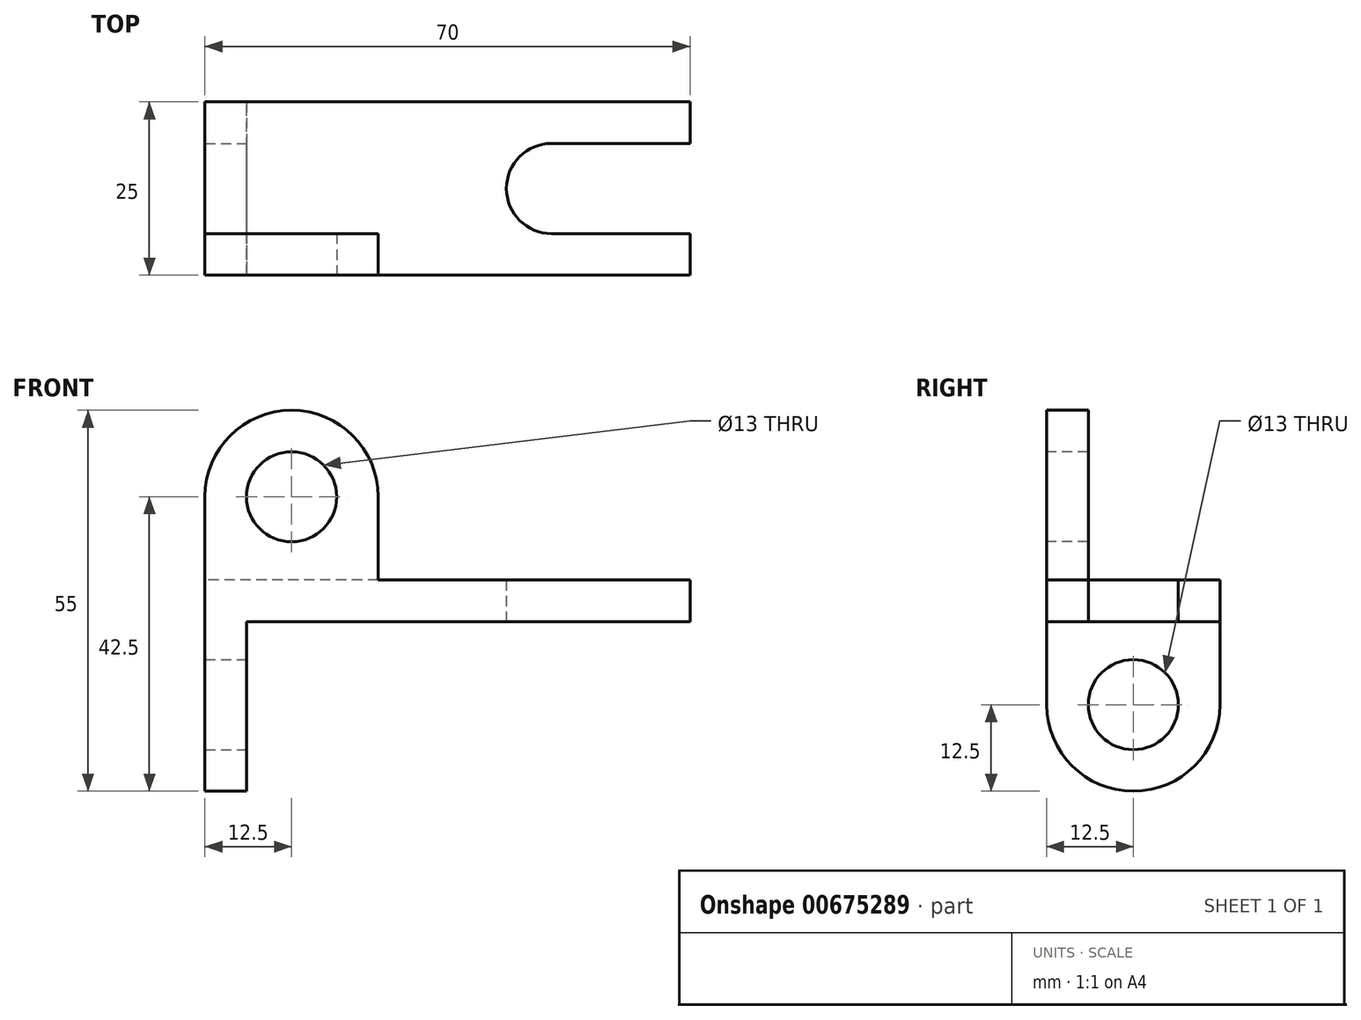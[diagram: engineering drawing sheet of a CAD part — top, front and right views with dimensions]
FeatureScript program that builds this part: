
annotation { "Feature Type Name" : "Feature", "Feature Type Description" : "" }
export const myFeature = defineFeature(function(context is Context, id is Id, definition is map)
    precondition{}
    {
        {
            var Q0;
            Q0=qCreatedBy(makeId("Top.planeOp"),FACE);
            var sketch = newSketch(context, id + "F0", { "sketchPlane" : qUnion([Q0])});
            skLineSegment(sketch, "E0.bottom", {"start": v(32, -12.5) * mm, "end": v(-32, -12.5) * mm});
            skLineSegment(sketch, "E0.top", {"start": v(32, 12.5) * mm, "end": v(-32, 12.5) * mm});
            skLineSegment(sketch, "E0.left", {"start": v(32, -12.5) * mm, "end": v(32, 12.5) * mm});
            skLineSegment(sketch, "E0.right", {"start": v(-32, -12.5) * mm, "end": v(-32, 12.5) * mm});
            skPoint(sketch, "E0.middle", {"position": v(0, 0) * mm});
            skLineSegment(sketch, "E1.bottom", {"start": v(32, -6.5) * mm, "end": v(12, -6.5) * mm});
            skLineSegment(sketch, "E1.top", {"start": v(32, 6.5) * mm, "end": v(12, 6.5) * mm});
            skLineSegment(sketch, "E1.left", {"start": v(32, -6.5) * mm, "end": v(32, 6.5) * mm});
            skLineSegment(sketch, "E1.right", {"start": v(12, -6.5) * mm, "end": v(12, 6.5) * mm});
            skPoint(sketch, "E1.middle", {"position": v(22, 0) * mm});
            skCircle(sketch, "E2", {"center": v(12, 0) * mm, "radius": 6.5 * mm});
            skSolve(sketch);
        }
        {
            var Q0;
            {var subQ4=sQuery(id+"F0.wireOp",EDGE,"E0.bottom");Q0=makeQuery(id+"F0.imprint","IMPRINT",FACE,{"disambiguationData":[TD([[makeQuery(id+"F0.imprint","IMPRINT",EDGE,{"derivedFrom":subQ4}),-1.0]])]});}
            extrude(context, id + "F1", {"entities" : qUnion([Q0]), "depth" : 6 * mm, "offsetDistance" : 25 * mm});
        }
        {
            var Q0;
            Q0=makeQuery(id+"F1.opExtrude","SWEPT_FACE",FACE,{"disambiguationData":[OSD([sQuery(id+"F0.wireOp",EDGE,"E0.right")])]});
            var sketch = newSketch(context, id + "F2", { "sketchPlane" : qUnion([Q0])});
            skLineSegment(sketch, "E3.bottom", {"start": v(-12.5, 6) * mm, "end": v(12.5, 6) * mm});
            skLineSegment(sketch, "E3.top", {"start": v(-12.5, -12) * mm, "end": v(12.5, -12) * mm});
            skLineSegment(sketch, "E3.left", {"start": v(-12.5, 6) * mm, "end": v(-12.5, -12) * mm});
            skLineSegment(sketch, "E3.right", {"start": v(12.5, 6) * mm, "end": v(12.5, -12) * mm});
            skCircle(sketch, "E4", {"center": v(0, -12) * mm, "radius": 12.5 * mm});
            skCircle(sketch, "E5", {"center": v(0, -12) * mm, "radius": 6.5 * mm});
            skSolve(sketch);
        }
        {
            var Q0;
            Q0 = qSketchRegion(id + "F2", true);
            extrude(context, id + "F3", {"entities" : qUnion([Q0]), "operationType" : NewBodyOperationType.ADD, "depth" : 6 * mm, "offsetDistance" : 25 * mm});
        }
        {
            var Q0;
            Q0=makeQuery(id+"F3.boolean.opBoolean","MERGE",FACE,{"derivedFrom":[makeQuery(id+"F1.opExtrude","SWEPT_FACE",FACE,{"disambiguationData":[OSD([sQuery(id+"F0.wireOp",EDGE,"E0.bottom")])]}),makeQuery(id+"F3.opExtrude","SWEPT_FACE",FACE,{"disambiguationData":[OSD([sQuery(id+"F2.wireOp",EDGE,"E3.right")])]})]});
            var sketch = newSketch(context, id + "F4", { "sketchPlane" : qUnion([Q0])});
            skLineSegment(sketch, "E6.bottom", {"start": v(-38, 0) * mm, "end": v(-13, 0) * mm});
            skLineSegment(sketch, "E6.top", {"start": v(-38, 18) * mm, "end": v(-13, 18) * mm});
            skLineSegment(sketch, "E6.left", {"start": v(-38, 0) * mm, "end": v(-38, 18) * mm});
            skLineSegment(sketch, "E6.right", {"start": v(-13, 0) * mm, "end": v(-13, 18) * mm});
            skArc(sketch, "E7", {"start": v(-13, 18) * mm, "mid": v(-25.5, 30.5) * mm, "end": v(-38, 18) * mm});
            skSolve(sketch);
        }
        {
            var Q0;
            {var subQ0=sQuery(id+"F4.wireOp",EDGE,"E6.top");Q0=makeQuery(id+"F4.imprint","IMPRINT",FACE,{"disambiguationData":[TD([[makeQuery(id+"F4.imprint","IMPRINT",EDGE,{"derivedFrom":subQ0}),-1.0]])]});}
            var Q1;
            Q1=makeQuery(id+"F4.imprint","IMPRINT",FACE,{"disambiguationData":[TD([[makeQuery(id+"F4.imprint","IMPRINT",EDGE,{"derivedFrom":sQuery(id+"F4.wireOp",EDGE,"E6.top")}),1.0]])]});
            extrude(context, id + "F5", {"entities" : qUnion([Q0, Q1]), "operationType" : NewBodyOperationType.ADD, "oppositeDirection" : true, "depth" : 6 * mm, "offsetDistance" : 25 * mm});
        }
        {
            var Q0;
            Q0=sQuery(id+"F4.wireOp",VERTEX,"E7.center");
            var Q1;
            Q1=makeQuery(id+"F1.opExtrude","SWEPT_BODY",BODY,{"disambiguationData":[OSD([sQuery(id+"F0.wireOp",EDGE,"E0.bottom"),sQuery(id+"F0.wireOp",EDGE,"E0.top"),sQuery(id+"F0.wireOp",EDGE,"E0.left"),sQuery(id+"F0.wireOp",EDGE,"E0.right"),sQuery(id+"F0.wireOp",EDGE,"E1.bottom"),sQuery(id+"F0.wireOp",EDGE,"E1.top"),sQuery(id+"F0.wireOp",EDGE,"E2")])]});
            hole(context, id + "F6", {"style" : HoleStyle.SIMPLE, "endStyle" : HoleEndStyle.THROUGH, "holeDiameter" : 13 * mm, "majorDiameter" : 5 * mm, "isTappedThrough" : true, "tappedDepth" : 12 * mm, "tapClearance" : 3, "locations" : qUnion([Q0]), "scope" : qUnion([Q1])});
        }
    });
